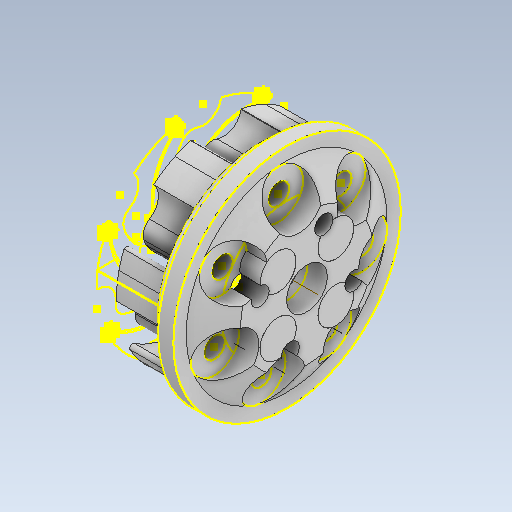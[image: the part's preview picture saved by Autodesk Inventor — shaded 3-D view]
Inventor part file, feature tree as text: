
AUTODESK INVENTOR PART (.ipt)
format: ipt  version: 2020 (Build 240168000, 168)  size: 635,392 bytes
history: native  units: in
note: dims shown in document units (in); Inventor stores cm internally (conversion verified against a paired STEP export)
features: sketch x16, other x4, plane x2
ambient origin geometry x8: Origin, YZ Plane, XZ Plane, XY Plane, X Axis, Y Axis, Z Axis, Center Point
bodies: Solid1 (feature_tree)
feature tree (22):
  other  "GoodAdap.ipt"
  other  "Solid1::GoodAdap.ipt"
  other  "TaggingFeature1"
  sketch  "Sketch1"  dims[d0=0.3937in]
  sketch  "Sketch3"
  sketch  "Sketch4"
  sketch  "Sketch5"
  sketch  "Sketch6"
  sketch  "Sketch7"
  sketch  "Sketch8"
  sketch  "Sketch9"
  sketch  "Sketch10"
  sketch  "Sketch11"
  sketch  "Sketch12"
  sketch  "Sketch14"
  sketch  "Sketch16"
  sketch  "Sketch17"
  sketch  "Sketch18"
  sketch  "Sketch19"
  plane  "Work Plane1"
  plane  "Work Plane2"
  other  "Work Axis1"
